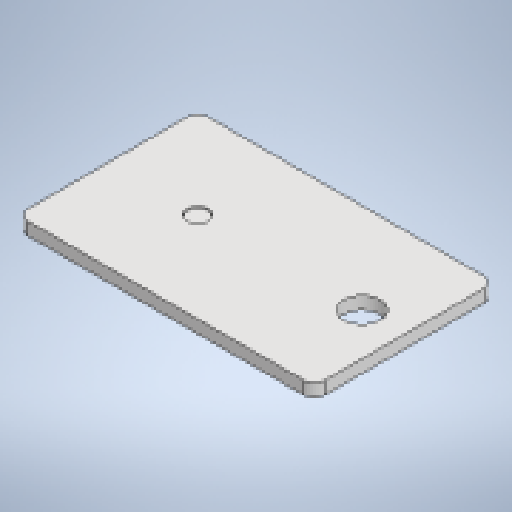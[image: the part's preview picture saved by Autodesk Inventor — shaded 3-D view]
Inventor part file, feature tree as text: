
AUTODESK INVENTOR PART (.ipt)
format: ipt  version: 2025.1 (Build 291241020, 241B)  size: 181,248 bytes
history: native  units: mm
features: sketch x2, other x2, sheet_metal_op x1, extrude x1, chamfer x1
ambient origin geometry x8: Origin, YZ Plane, XZ Plane, XY Plane, X Axis, Y Axis, Z Axis, Center Point
bodies: Solid1 (feature_tree)
feature tree (7):
  sheet_metal_op  "Face1"
  extrude  "Extrusion2"  Depth=85.0mm
  chamfer  "Corner Round2"
  sketch  "Sketch1"  dims[d0=150.0mm d1=85.0mm]
  other  "Plate1"
  sketch  "Sketch5"  dims[d2=6.0mm d23=17.0mm d25=20.0mm d26=20.0mm d27=10.0mm d28=1.0mm d29=0.0mm d33=5.0mm]
  other  "Definition1"
